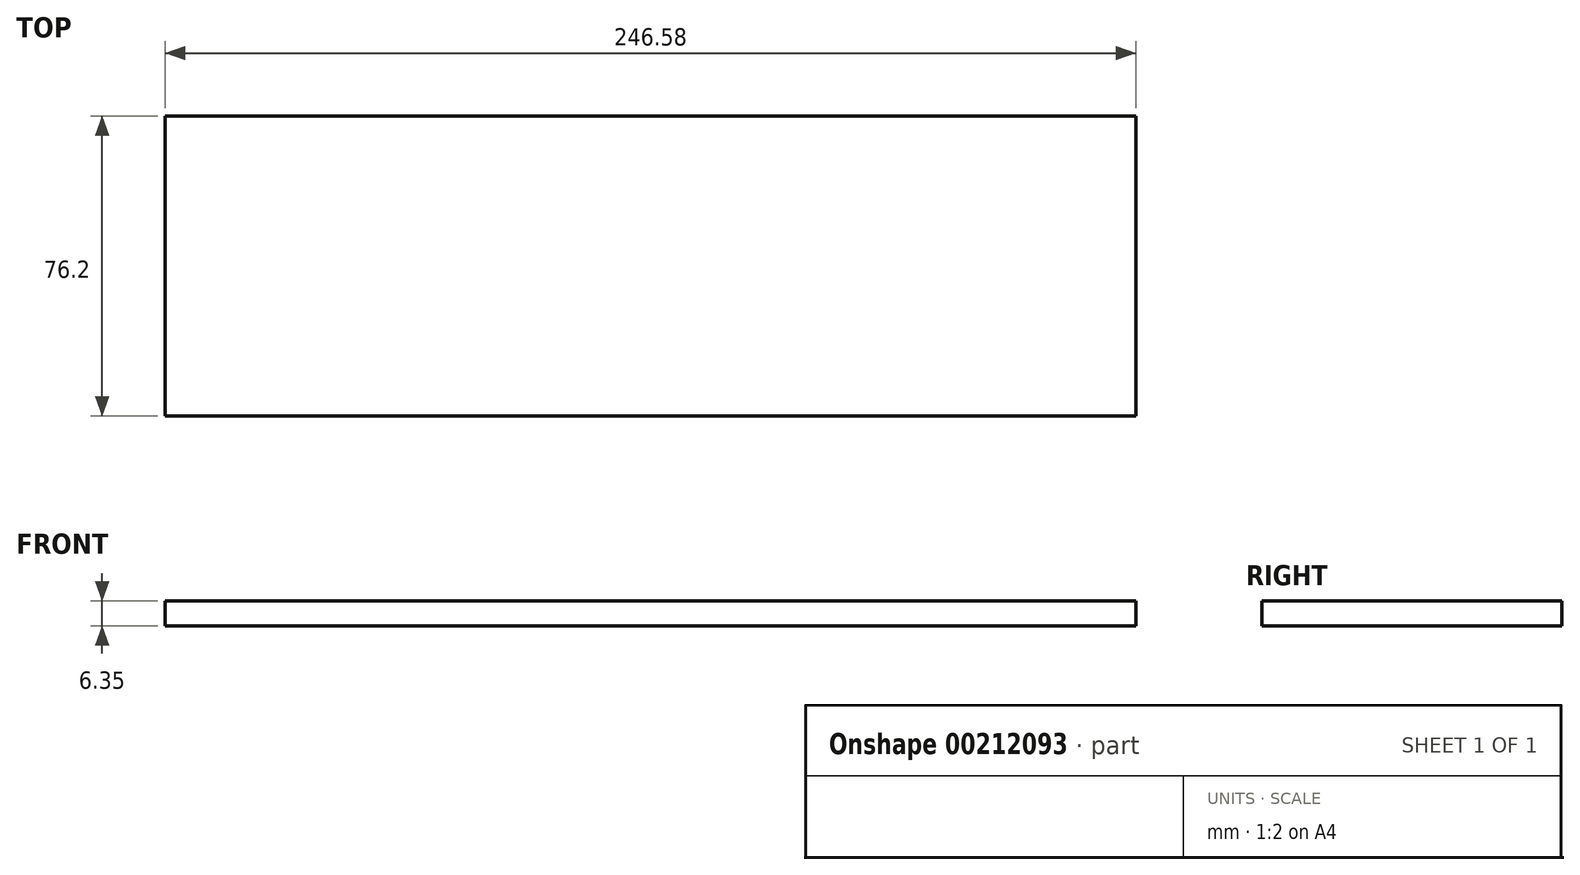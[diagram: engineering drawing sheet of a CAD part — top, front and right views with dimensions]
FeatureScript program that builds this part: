
annotation { "Feature Type Name" : "Feature", "Feature Type Description" : "" }
export const myFeature = defineFeature(function(context is Context, id is Id, definition is map)
    precondition{}
    {
        {
            var Q0;
            Q0=qCreatedBy(makeId("Top.planeOp"),FACE);
            var sketch = newSketch(context, id + "F0", { "sketchPlane" : qUnion([Q0])});
            skLineSegment(sketch, "E0.bottom", {"start": v(-111.05, 0) * mm, "end": v(135.53, 0) * mm});
            skLineSegment(sketch, "E0.top", {"start": v(-111.05, 76.2) * mm, "end": v(135.53, 76.2) * mm});
            skLineSegment(sketch, "E0.left", {"start": v(-111.05, 0) * mm, "end": v(-111.05, 76.2) * mm});
            skLineSegment(sketch, "E0.right", {"start": v(135.53, 0) * mm, "end": v(135.53, 76.2) * mm});
            skSolve(sketch);
        }
        {
            var Q0;
            Q0=makeQuery(id+"F0.imprint","IMPRINT",FACE,{"disambiguationData":[TD([[makeQuery(id+"F0.imprint","IMPRINT",EDGE,{"derivedFrom":sQuery(id+"F0.wireOp",EDGE,"E0.bottom")}),1.0]])]});
            extrude(context, id + "F1", {"entities" : qUnion([Q0]), "depth" : 6.35 * mm});
        }
    });
